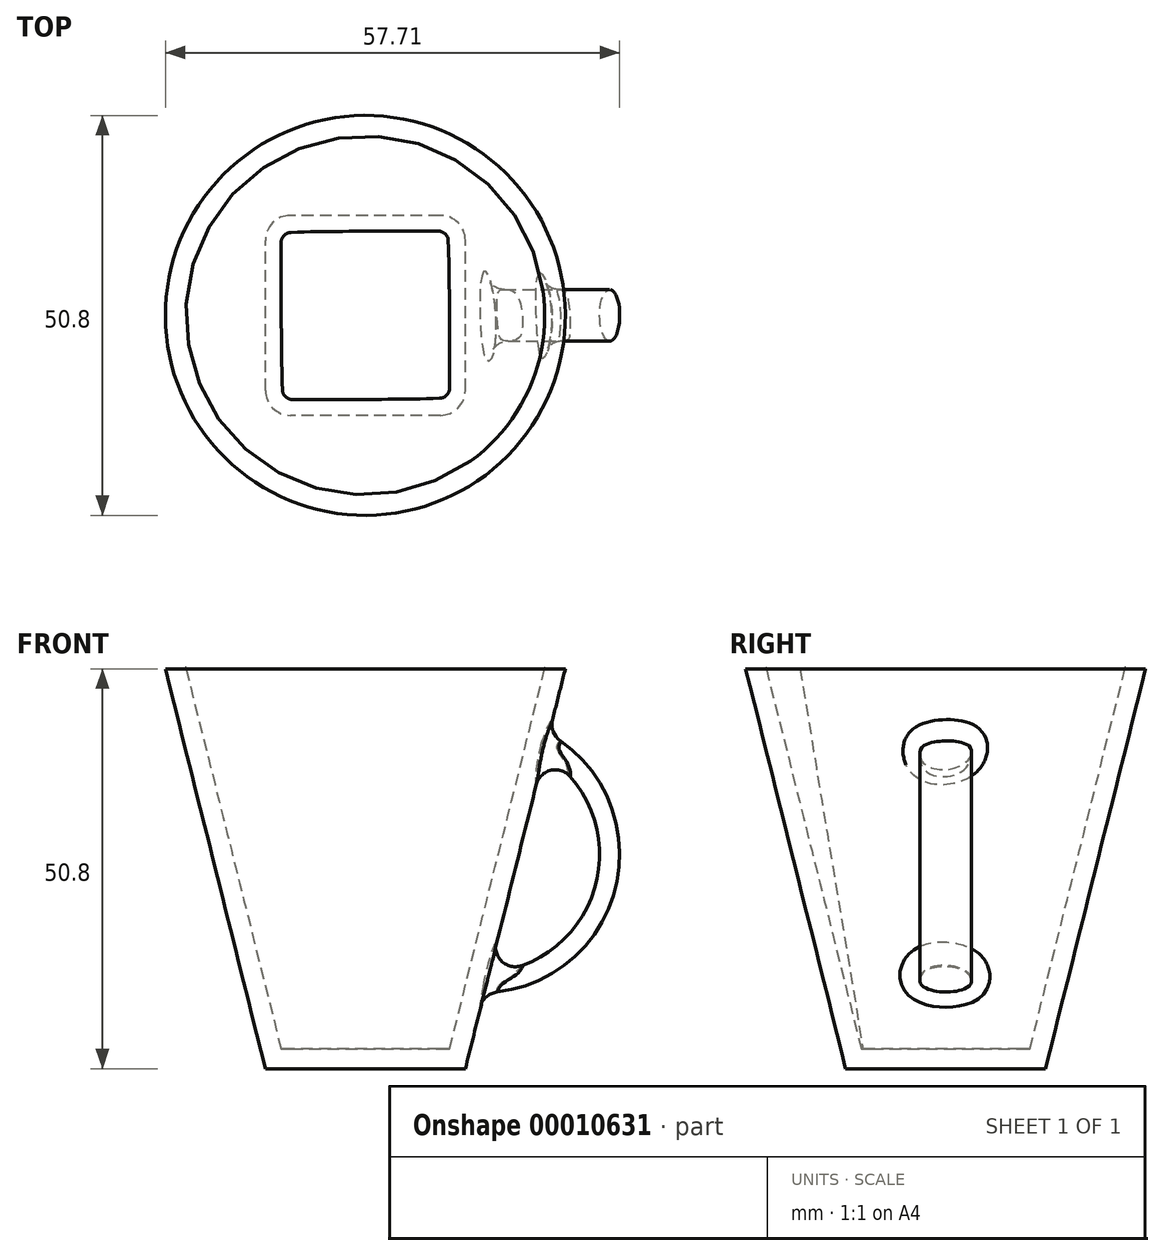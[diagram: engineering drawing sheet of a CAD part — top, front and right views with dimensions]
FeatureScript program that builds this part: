
annotation { "Feature Type Name" : "Feature", "Feature Type Description" : "" }
export const myFeature = defineFeature(function(context is Context, id is Id, definition is map)
    precondition{}
    {
        {
            var Q0;
            Q0=qCreatedBy(makeId("Top.planeOp"),FACE);
            var sketch = newSketch(context, id + "F0", { "sketchPlane" : qUnion([Q0])});
            skLineSegment(sketch, "E0.rect.bottom", {"start": v(9.52, -12.7) * mm, "end": v(-9.53, -12.7) * mm});
            skLineSegment(sketch, "E0.rect.top", {"start": v(9.52, 12.7) * mm, "end": v(-9.53, 12.7) * mm});
            skLineSegment(sketch, "E0.rect.left", {"start": v(12.7, -9.52) * mm, "end": v(12.7, 9.53) * mm});
            skLineSegment(sketch, "E0.rect.right", {"start": v(-12.7, -9.53) * mm, "end": v(-12.7, 9.53) * mm});
            skPoint(sketch, "E0.rect.middle", {"position": v(0, 0) * mm});
            skPoint(sketch, "E1.visualSharp", {"position": v(-12.7, 12.7) * mm});
            skArc(sketch, "E1.filletArc", {"start": v(-9.53, 12.7) * mm, "mid": v(-11.77, 11.77) * mm, "end": v(-12.7, 9.53) * mm});
            skPoint(sketch, "E2.visualSharp", {"position": v(12.7, -12.7) * mm});
            skArc(sketch, "E2.filletArc", {"start": v(9.52, -12.7) * mm, "mid": v(11.77, -11.77) * mm, "end": v(12.7, -9.52) * mm});
            skPoint(sketch, "E3.visualSharp", {"position": v(12.7, 12.7) * mm});
            skArc(sketch, "E3.filletArc", {"start": v(12.7, 9.53) * mm, "mid": v(11.77, 11.77) * mm, "end": v(9.52, 12.7) * mm});
            skPoint(sketch, "E4.visualSharp", {"position": v(-12.7, -12.7) * mm});
            skArc(sketch, "E4.filletArc", {"start": v(-12.7, -9.53) * mm, "mid": v(-11.77, -11.77) * mm, "end": v(-9.53, -12.7) * mm});
            skSolve(sketch);
        }
        {
            var Q0;
            Q0=qCreatedBy(makeId("Top.planeOp"),FACE);
            cPlane(context, id + "F1", {"entities" : qUnion([Q0]), "cplaneType" : CPlaneType.OFFSET, "offset" : 50.8 * mm, "width" : 152.4 * mm, "height" : 152.4 * mm});
        }
        {
            var Q0;
            Q0=qCreatedBy(id+"F1.planeOp",FACE);
            var sketch = newSketch(context, id + "F2", { "sketchPlane" : qUnion([Q0])});
            skCircle(sketch, "E5", {"center": v(0, 0) * mm, "radius": 25.4 * mm});
            skSolve(sketch);
        }
        {
            var Q0;
            Q0 = qSketchRegion(id + "F2", true);
            var Q1;
            Q1 = qSketchRegion(id + "F0", true);
            loft(context, id + "F3", {"sheetProfilesArray" : [{ "sheetProfileEntities" : qUnion([Q0]) }, { "sheetProfileEntities" : qUnion([Q1]) }]});
        }
        {
            var Q0;
            Q0=makeQuery(id+"F3.opLoft","CAP_FACE",FACE,{"disambiguationData":[OSD([makeQuery(id+"F2.imprint","IMPRINT",FACE,{"disambiguationData":[TD([[makeQuery(id+"F2.imprint","IMPRINT",EDGE,{"derivedFrom":sQuery(id+"F2.wireOp",EDGE,"E5")}),1.0]])]})])],"isStart":true});
            shell(context, id + "F4", {"entities" : qUnion([Q0]), "thickness" : 2.54 * mm});
        }
        {
            var Q0;
            Q0=qCreatedBy(makeId("Right.planeOp"),FACE);
            cPlane(context, id + "F5", {"entities" : qUnion([Q0]), "cplaneType" : CPlaneType.OFFSET, "offset" : 14.73 * mm, "width" : 152.4 * mm, "height" : 152.4 * mm});
        }
        {
            var Q0;
            Q0=qCreatedBy(id+"F5.planeOp",FACE);
            var sketch = newSketch(context, id + "F6", { "sketchPlane" : qUnion([Q0])});
            skEllipse(sketch, "E6", {"center": v(0, 10.9) * mm, "majorRadius": 3.28 * mm, "minorRadius": 1.28 * mm, "majorAxis": v(1, 0)});
            skLineSegment(sketch, "E7", {"start": v(-8.6, 27.2) * mm, "end": v(11.78, 27.2) * mm});
            skSolve(sketch);
        }
        {
            var Q0;
            Q0=makeQuery(id+"F6.imprint","IMPRINT",FACE,{"disambiguationData":[TD([[makeQuery(id+"F6.imprint","IMPRINT",EDGE,{"derivedFrom":sQuery(id+"F6.wireOp",EDGE,"E6")}),1.0]])]});
            var Q1;
            Q1=sQuery(id+"F6.wireOp",EDGE,"E7");
            revolve(context, id + "F7", {"operationType" : NewBodyOperationType.ADD, "entities" : qUnion([Q0]), "axis" : qUnion([Q1]), "revolveType" : RevolveType.ONE_DIRECTION, "oppositeDirection" : true, "angle" : 156.1 * degree});
        }
        {
            var Q0;
            Q0=makeQuery(id+"F7.boolean.opBoolean","INTERSECT",EDGE,{"disambiguationData":[OD(0.0)],"derivedFrom":[makeQuery(id+"F3.opLoft","SWEPT_FACE",FACE,{"disambiguationData":[OSD([sQuery(id+"F0.wireOp",EDGE,"E0.rect.bottom"),sQuery(id+"F0.wireOp",EDGE,"E2.filletArc"),sQuery(id+"F0.wireOp",EDGE,"E4.filletArc"),sQuery(id+"F2.wireOp",EDGE,"E5")])]}),makeQuery(id+"F7.opRevolve","SWEPT_FACE",FACE,{"disambiguationData":[OSD([sQuery(id+"F6.wireOp",EDGE,"E6")])]})]});
            var Q1;
            Q1=makeQuery(id+"F7.boolean.opBoolean","INTERSECT",EDGE,{"disambiguationData":[OD(1.0)],"derivedFrom":[makeQuery(id+"F3.opLoft","SWEPT_FACE",FACE,{"disambiguationData":[OSD([sQuery(id+"F0.wireOp",EDGE,"E0.rect.bottom"),sQuery(id+"F0.wireOp",EDGE,"E2.filletArc"),sQuery(id+"F0.wireOp",EDGE,"E4.filletArc"),sQuery(id+"F2.wireOp",EDGE,"E5")])]}),makeQuery(id+"F7.opRevolve","SWEPT_FACE",FACE,{"disambiguationData":[OSD([sQuery(id+"F6.wireOp",EDGE,"E6")])]})]});
            fillet(context, id + "F8", {"entities" : qUnion([Q0, Q1]), "radius" : 2.54 * mm, "tangentPropagation" : true, "allowEdgeOverflow" : false});
        }
    });
